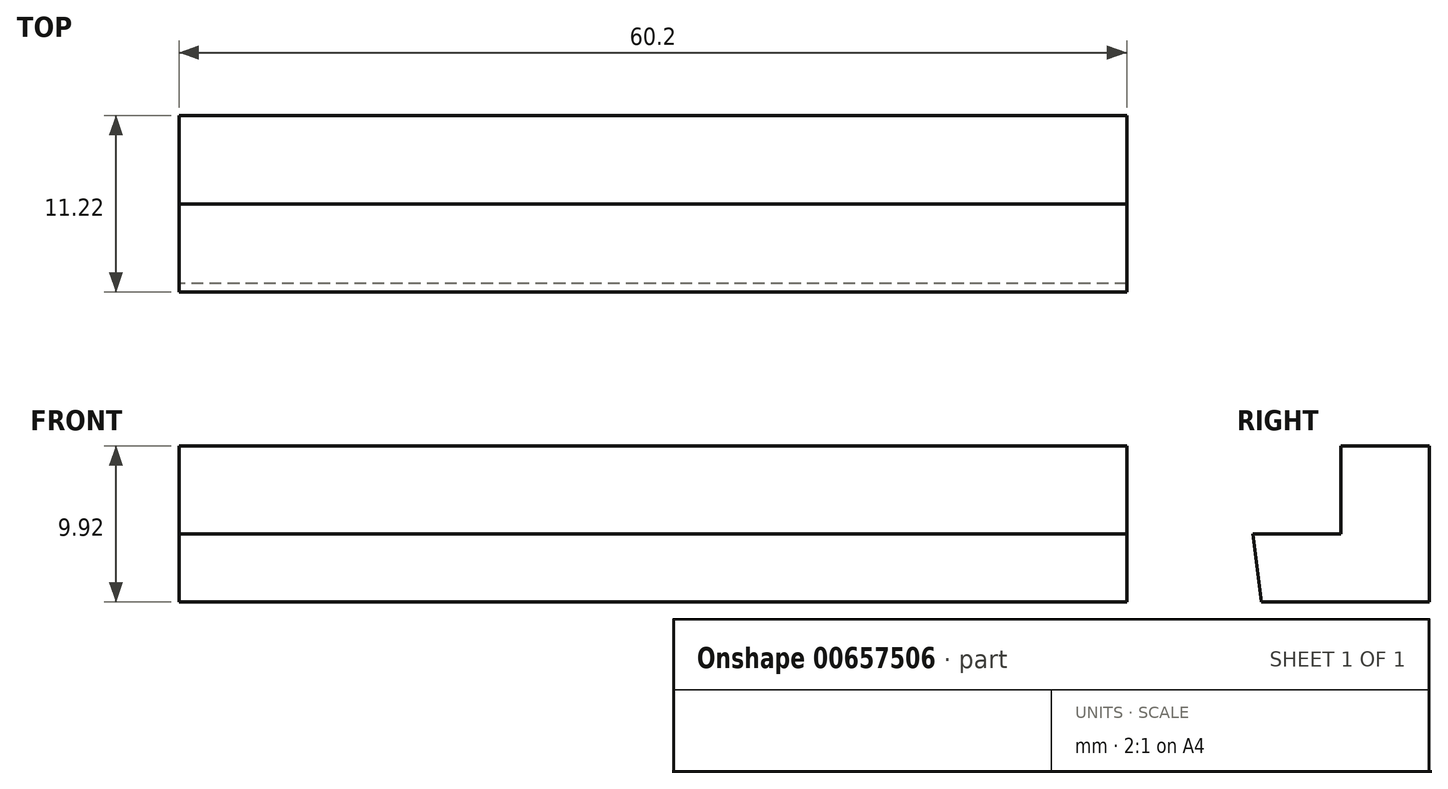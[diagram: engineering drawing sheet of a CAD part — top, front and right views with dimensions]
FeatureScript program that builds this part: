
annotation { "Feature Type Name" : "Feature", "Feature Type Description" : "" }
export const myFeature = defineFeature(function(context is Context, id is Id, definition is map)
    precondition{}
    {
        {
            var Q0;
            Q0=qCreatedBy(makeId("Right.planeOp"),FACE);
            var sketch = newSketch(context, id + "F0", { "sketchPlane" : qUnion([Q0])});
            skLineSegment(sketch, "E0", {"start": v(-42.34, -27.88) * mm, "end": v(-31.12, -27.88) * mm});
            skLineSegment(sketch, "E1", {"start": v(-31.12, -27.88) * mm, "end": v(-31.12, -17.96) * mm});
            skLineSegment(sketch, "E2", {"start": v(-31.12, -17.96) * mm, "end": v(-36.73, -17.96) * mm});
            skLineSegment(sketch, "E3", {"start": v(-36.73, -17.96) * mm, "end": v(-36.73, -23.55) * mm});
            skLineSegment(sketch, "E4", {"start": v(-36.73, -23.55) * mm, "end": v(-42.34, -23.55) * mm});
            skLineSegment(sketch, "E5", {"start": v(-42.34, -23.55) * mm, "end": v(-41.78, -27.88) * mm});
            skSolve(sketch);
        }
        {
            var Q0;
            {var subQ0=sQuery(id+"F0.wireOp",EDGE,"E1");Q0=makeQuery(id+"F0.imprint","IMPRINT",FACE,{"disambiguationData":[TD([[makeQuery(id+"F0.imprint","IMPRINT",EDGE,{"derivedFrom":subQ0}),1.0]])]});}
            extrude(context, id + "F1", {"entities" : qUnion([Q0]), "depth" : 60.2 * mm, "offsetDistance" : 25.4 * mm});
        }
    });
